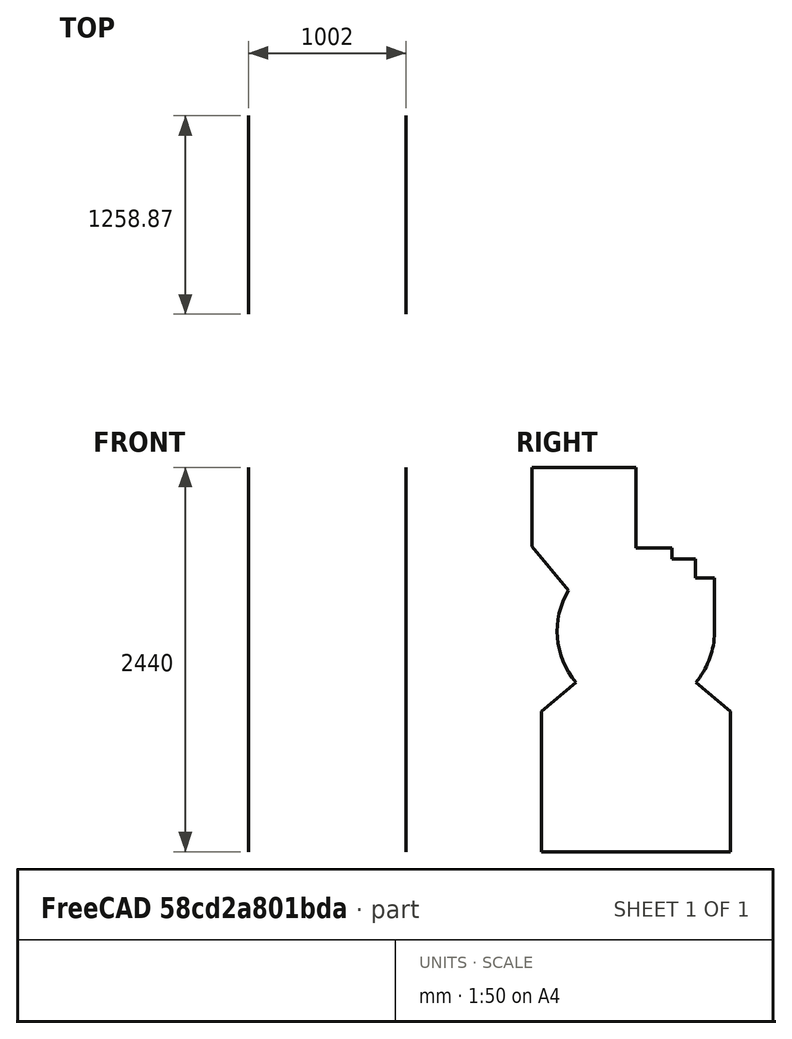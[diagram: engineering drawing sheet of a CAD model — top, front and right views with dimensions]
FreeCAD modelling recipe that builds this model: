
FCSTD DOCUMENT
Label: Shell_all
objects: Sketcher::SketchObject×3, PartDesign::Pad×3
note: 9 computed .brp shape members not serialized (recipe doc carries the construction recipe); baked Part::Feature solids carry a one-line shape summary decoded from their .brp

FEATURE [Sketcher::SketchObject] Sketch  label="Shell "
  Placement = pos=(-500,0,0) rot=(0.57735,0.57735,0.57735;2.0944rad)
  sketch-geometry (20):
    g0: LineSegment StartX=-420.968 StartY=257.478 StartZ=0 EndX=-649.678 EndY=540 EndZ=0
    g1: LineSegment StartX=0 StartY=530 StartZ=0 EndX=230 EndY=530 EndZ=0
    g2: LineSegment StartX=230 StartY=530 StartZ=0 EndX=230 EndY=460 EndZ=0
    g3: LineSegment StartX=230 StartY=460 StartZ=0 EndX=380 EndY=460 EndZ=0
    g4: LineSegment StartX=380 StartY=460 StartZ=0 EndX=380 EndY=340 EndZ=0
    g5: LineSegment StartX=380 StartY=340 StartZ=0 EndX=503.198 EndY=340 EndZ=0
    g6: LineSegment StartX=503.198 StartY=340 StartZ=0 EndX=503.198 EndY=-30 EndZ=0
    g7: LineSegment StartX=-649.678 StartY=1040 StartZ=0 EndX=-649.678 EndY=540 EndZ=0
    g8: LineSegment StartX=0 StartY=530 StartZ=0 EndX=-230 EndY=470 EndZ=0
    g9: LineSegment StartX=-381.851 StartY=-324.642 StartZ=0 EndX=-600 EndY=-507.691 EndZ=0
    g10: LineSegment StartX=-600 StartY=-507.691 StartZ=0 EndX=-600 EndY=-1400 EndZ=0
    g11: LineSegment StartX=-600 StartY=-1400 StartZ=0 EndX=600 EndY=-1400 EndZ=0
    g12: LineSegment StartX=600 StartY=-1400 StartZ=0 EndX=600 EndY=-507.691 EndZ=0
    g13: LineSegment StartX=600 StartY=-507.691 StartZ=0 EndX=386.273 EndY=-328.353 EndZ=0
    g14: LineSegment StartX=-649.678 StartY=1040 StartZ=0 EndX=0 EndY=1040 EndZ=0
    g15: LineSegment StartX=0 StartY=1040 StartZ=0 EndX=0 EndY=530 EndZ=0
    g16: ArcOfCircle CenterX=3.75731 CenterY=-6.3561 CenterZ=0 NormalX=0 NormalY=0 NormalZ=1 Radius=500 StartAngle=5.58348 EndAngle=6.23588
    g17: ArcOfCircle CenterX=3.75731 CenterY=-6.3561 CenterZ=0 NormalX=0 NormalY=0 NormalZ=1 Radius=500 StartAngle=2.58574 EndAngle=3.83164
    g18: ArcOfCircle CenterX=3.75731 CenterY=-6.3561 CenterZ=0 NormalX=0 NormalY=0 NormalZ=1 Radius=500 StartAngle=3.83164 EndAngle=4.69487
    g19: ArcOfCircle CenterX=3.75731 CenterY=-6.3561 CenterZ=0 NormalX=0 NormalY=0 NormalZ=1 Radius=500 StartAngle=4.71487 EndAngle=5.58348
  constraints (61):
    c: Horizontal(g1)
    c: Vertical(g2)
    c: Coincident(g3,g2)
    c: Horizontal(g3)
    c: Vertical(g4)
    c: Coincident(g5,g4)
    c: Horizontal(g5)
    c: DistanceY(g0) = 540
    c: Coincident(g1,g2)
    c: Coincident(g3,g4)
    c: Vertical(g6)
    c: Distance(g6) = 370
    c: Coincident(g7,g0)
    c: Vertical(g7)
    c: Distance(g0) = 363.493
    c: Distance(g7) = 500
    c: Coincident(g10,g9)
    c: Vertical(g10)
    c: Horizontal(g11)
    c: Coincident(g12,g11)
    c: Vertical(g12)
    c: Coincident(g13,g12)
    c: Coincident(g11,g10)
    c: Equal(g12,g10)
    c: DistanceX(g11) = 600
    c: DistanceY(g11) = -1400
    c: Angle(g10,g9) = 2.26893
    c: Angle(g13,g12) = 2.26893
    c: Distance(g10) = 892.309
    c: Distance(g11) = 1200
    c: Coincident(g14,g7)
    c: Horizontal(g14)
    c: Coincident(g15,g14)
    c: Vertical(g15)
    c: Coincident(g5,g6)
    c: Coincident(g8,g1)
    c: Coincident(g15,g1)
    c: DistanceX(g4) = 380
    c: DistanceY(g4) = 340
    c: DistanceX(g2) = 230
    c: DistanceY(g2) = 460
    c: DistanceX(g1) = 0
    c: DistanceY(g1) = 530
    c: DistanceX(g8) = -230
    c: DistanceY(g8) = 470
    c: Coincident(g16,g6)
    c: Coincident(g16,g13)
    c: Coincident(g17,g16)
    c: Coincident(g17,g0)
    c: Coincident(g17,g9)
    c: Radius(g17) = 500
    c: Radius(g16) = 500
    c: DistanceX(g13) = 386.273
    c: DistanceX(g9) = -381.851
    c: DistanceY(g0) = 257.478
    c: Coincident(g18,g16)
    c: Coincident(g18,g9)
    c: Coincident(g19,g16)
    c: Coincident(g19,g13)
    c: DistanceX(g19) = 5
    c: DistanceX(g18) = -5
FEATURE [Sketcher::SketchObject] Sketch001  label="Shell_back"
  Placement = pos=(-500,0,0) rot=(0.57735,0.57735,0.57735;2.0944rad)
  sketch-geometry (17):
    g0: ArcOfCircle CenterX=0 CenterY=0 CenterZ=0 NormalX=0 NormalY=0 NormalZ=1 Radius=500 StartAngle=2.59474 EndAngle=3.84621
    g1: LineSegment StartX=-427.083 StartY=260 StartZ=0 EndX=-658.874 EndY=540 EndZ=0
    g2: LineSegment StartX=0 StartY=530 StartZ=0 EndX=230 EndY=530 EndZ=0
    g3: LineSegment StartX=230 StartY=530 StartZ=0 EndX=230 EndY=460 EndZ=0
    g4: LineSegment StartX=230 StartY=460 StartZ=0 EndX=380 EndY=460 EndZ=0
    g5: LineSegment StartX=380 StartY=460 StartZ=0 EndX=380 EndY=340 EndZ=0
    g6: LineSegment StartX=380 StartY=340 StartZ=0 EndX=499.438 EndY=340 EndZ=0
    g7: LineSegment StartX=499.438 StartY=340 StartZ=0 EndX=499.438 EndY=-23.6939 EndZ=0
    g8: LineSegment StartX=-658.874 StartY=1040 StartZ=0 EndX=-658.874 EndY=540 EndZ=0
    g9: LineSegment StartX=-380.931 StartY=-323.87 StartZ=0 EndX=-600 EndY=-507.691 EndZ=0
    g10: LineSegment StartX=-600 StartY=-507.691 StartZ=0 EndX=-600 EndY=-1400 EndZ=0
    g11: LineSegment StartX=-600 StartY=-1400 StartZ=0 EndX=600 EndY=-1400 EndZ=0
    g12: LineSegment StartX=600 StartY=-1400 StartZ=0 EndX=600 EndY=-507.691 EndZ=0
    g13: LineSegment StartX=600 StartY=-507.691 StartZ=0 EndX=380.931 EndY=-323.87 EndZ=0
    g14: ArcOfCircle CenterX=0 CenterY=0 CenterZ=0 NormalX=0 NormalY=0 NormalZ=1 Radius=500 StartAngle=5.57857 EndAngle=6.23578
    g15: LineSegment StartX=-658.874 StartY=1040 StartZ=0 EndX=0 EndY=1040 EndZ=0
    g16: LineSegment StartX=0 StartY=1040 StartZ=0 EndX=0 EndY=530 EndZ=0
  constraints (52):
    c: Radius(g0) = 500
    c: DistanceX(g0) = 0
    c: DistanceY(g0) = 0
    c: Horizontal(g2)
    c: Vertical(g3)
    c: Coincident(g4,g3)
    c: Horizontal(g4)
    c: Vertical(g5)
    c: Coincident(g6,g5)
    c: Horizontal(g6)
    c: DistanceY(g1) = 540
    c: Coincident(g2,g3)
    c: Coincident(g4,g5)
    c: Vertical(g7)
    c: Coincident(g1,g0)
    c: Coincident(g8,g1)
    c: Vertical(g8)
    c: Distance(g1) = 363.493
    c: Distance(g8) = 500
    c: Coincident(g10,g9)
    c: Vertical(g10)
    c: Horizontal(g11)
    c: Coincident(g12,g11)
    c: Vertical(g12)
    c: Coincident(g13,g12)
    c: Coincident(g11,g10)
    c: Equal(g12,g10)
    c: DistanceX(g11) = 600
    c: DistanceY(g11) = -1400
    c: Angle(g10,g9) = 2.26893
    c: Angle(g13,g12) = 2.26893
    c: Distance(g10) = 892.309
    c: Distance(g11) = 1200
    c: Equal(g0,g14)
    c: Coincident(g0,g14)
    c: Coincident(g15,g8)
    c: Horizontal(g15)
    c: Coincident(g16,g15)
    c: Vertical(g16)
    c: Coincident(g6,g7)
    c: Coincident(g16,g2)
    c: DistanceX(g5) = 380
    c: DistanceY(g5) = 340
    c: DistanceX(g3) = 230
    c: DistanceY(g3) = 460
    c: DistanceX(g2) = 0
    c: DistanceY(g2) = 530
    c: DistanceY(g0) = 260
    c: Coincident(g9,g0)
    c: Coincident(g14,g13)
    c: Coincident(g14,g7)
    c: Distance(g7) = 363.694
FEATURE [PartDesign::Pad] Pad001  label="Shell_back_"
  Length = 1
  MirroredExtent = false
  Reversed = true
  Sketch = -> Sketch001
FEATURE [Sketcher::SketchObject] Sketch002  label="Shell_front"
  Placement = pos=(500,0,0) rot=(0.57735,0.57735,0.57735;2.0944rad)
  sketch-geometry (17):
    g0: ArcOfCircle CenterX=0 CenterY=0 CenterZ=0 NormalX=0 NormalY=0 NormalZ=1 Radius=500 StartAngle=2.59474 EndAngle=3.84621
    g1: LineSegment StartX=-427.083 StartY=260 StartZ=0 EndX=-658.874 EndY=540 EndZ=0
    g2: LineSegment StartX=0 StartY=530 StartZ=0 EndX=230 EndY=530 EndZ=0
    g3: LineSegment StartX=230 StartY=530 StartZ=0 EndX=230 EndY=460 EndZ=0
    g4: LineSegment StartX=230 StartY=460 StartZ=0 EndX=380 EndY=460 EndZ=0
    g5: LineSegment StartX=380 StartY=460 StartZ=0 EndX=380 EndY=340 EndZ=0
    g6: LineSegment StartX=380 StartY=340 StartZ=0 EndX=499.099 EndY=340 EndZ=0
    g7: LineSegment StartX=499.099 StartY=340 StartZ=0 EndX=499.099 EndY=-30 EndZ=0
    g8: LineSegment StartX=-658.874 StartY=1040 StartZ=0 EndX=-658.874 EndY=540 EndZ=0
    g9: LineSegment StartX=-380.931 StartY=-323.87 StartZ=0 EndX=-600 EndY=-507.691 EndZ=0
    g10: LineSegment StartX=-600 StartY=-507.691 StartZ=0 EndX=-600 EndY=-1400 EndZ=0
    g11: LineSegment StartX=-600 StartY=-1400 StartZ=0 EndX=600 EndY=-1400 EndZ=0
    g12: LineSegment StartX=600 StartY=-1400 StartZ=0 EndX=600 EndY=-507.691 EndZ=0
    g13: LineSegment StartX=600 StartY=-507.691 StartZ=0 EndX=380.931 EndY=-323.87 EndZ=0
    g14: ArcOfCircle CenterX=0 CenterY=0 CenterZ=0 NormalX=0 NormalY=0 NormalZ=1 Radius=500 StartAngle=5.57857 EndAngle=6.22315
    g15: LineSegment StartX=-658.874 StartY=1040 StartZ=0 EndX=0 EndY=1040 EndZ=0
    g16: LineSegment StartX=0 StartY=1040 StartZ=0 EndX=0 EndY=530 EndZ=0
  constraints (52):
    c: Radius(g0) = 500
    c: DistanceX(g0) = 0
    c: DistanceY(g0) = 0
    c: Horizontal(g2)
    c: Vertical(g3)
    c: Coincident(g4,g3)
    c: Horizontal(g4)
    c: Vertical(g5)
    c: Coincident(g6,g5)
    c: Horizontal(g6)
    c: DistanceY(g1) = 540
    c: Coincident(g2,g3)
    c: Coincident(g4,g5)
    c: Coincident(g7,g14)
    c: Vertical(g7)
    c: Distance(g7) = 370
    c: Coincident(g1,g0)
    c: Coincident(g8,g1)
    c: Vertical(g8)
    c: Distance(g1) = 363.493
    c: Distance(g8) = 500
    c: Coincident(g10,g9)
    c: Vertical(g10)
    c: Horizontal(g11)
    c: Coincident(g12,g11)
    c: Vertical(g12)
    c: Coincident(g13,g12)
    c: Coincident(g11,g10)
    c: Equal(g12,g10)
    c: DistanceX(g11) = 600
    c: DistanceY(g11) = -1400
    c: Angle(g10,g9) = 2.26893
    c: Angle(g13,g12) = 2.26893
    c: Distance(g10) = 892.309
    c: Distance(g11) = 1200
    c: Coincident(g0,g14)
    c: Coincident(g15,g8)
    c: Horizontal(g15)
    c: Coincident(g16,g15)
    c: Vertical(g16)
    c: Coincident(g6,g7)
    c: Coincident(g16,g2)
    c: DistanceX(g5) = 380
    c: DistanceY(g5) = 340
    c: DistanceX(g3) = 230
    c: DistanceY(g3) = 460
    c: DistanceX(g2) = 0
    c: DistanceY(g2) = 530
    c: DistanceY(g0) = 260
    c: Coincident(g9,g0)
    c: Radius(g14) = 500
    c: Coincident(g14,g13)
FEATURE [PartDesign::Pad] Pad002  label="Shell_front_"
  Length = 1
  MirroredExtent = false
  Sketch = -> Sketch002
FEATURE [PartDesign::Pad] Pad  label="Shell_"
  Length = 1000
  MirroredExtent = false
  Sketch = -> Sketch
